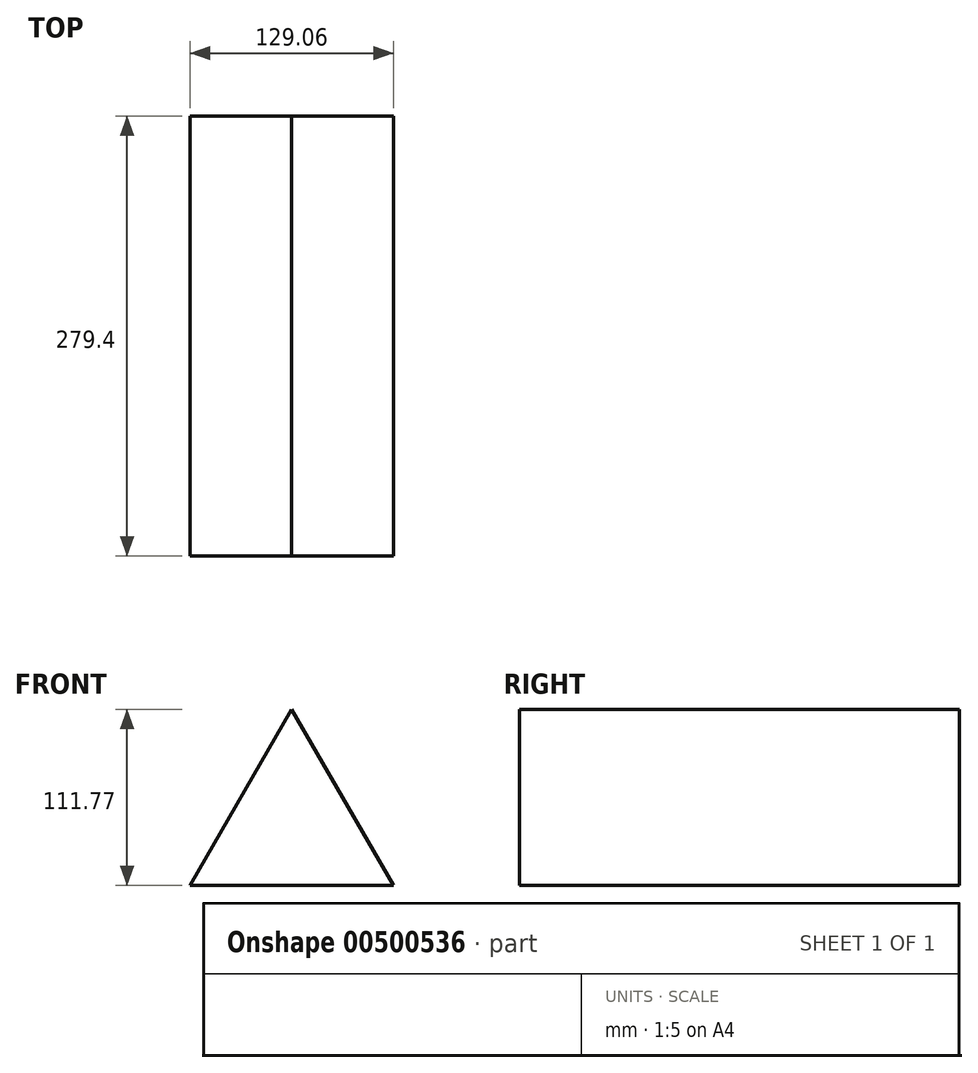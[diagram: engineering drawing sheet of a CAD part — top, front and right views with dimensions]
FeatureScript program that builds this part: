
annotation { "Feature Type Name" : "Feature", "Feature Type Description" : "" }
export const myFeature = defineFeature(function(context is Context, id is Id, definition is map)
    precondition{}
    {
        {
            var Q0;
            Q0=qCreatedBy(makeId("Front.planeOp"),FACE);
            var sketch = newSketch(context, id + "F0", { "sketchPlane" : qUnion([Q0])});
            skCircle(sketch, "E0.cCircle", {"center": v(0, 0) * mm, "radius": 74.51 * mm, "construction": true});
            skLineSegment(sketch, "E0.0", {"start": v(0, 74.51) * mm, "end": v(64.53, -37.26) * mm});
            skLineSegment(sketch, "E0.1", {"start": v(64.53, -37.26) * mm, "end": v(-64.53, -37.26) * mm});
            skLineSegment(sketch, "E0.2", {"start": v(-64.53, -37.26) * mm, "end": v(0, 74.51) * mm});
            skSolve(sketch);
        }
        {
            var Q0;
            Q0=makeQuery(id+"F0.imprint","IMPRINT",FACE,{"disambiguationData":[TD([[makeQuery(id+"F0.imprint","IMPRINT",EDGE,{"derivedFrom":sQuery(id+"F0.wireOp",EDGE,"E0.0")}),-1.0]])]});
            extrude(context, id + "F1", {"entities" : qUnion([Q0]), "depth" : 279.4 * mm});
        }
    });
